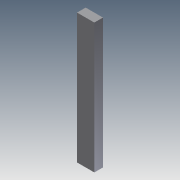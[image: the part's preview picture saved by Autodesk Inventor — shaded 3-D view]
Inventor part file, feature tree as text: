
AUTODESK INVENTOR PART (.ipt)
format: ipt  version: 2011 (Build 150239000, 239)  size: 657,920 bytes
history: native  units: in
note: dims shown in document units (in); Inventor stores cm internally (conversion verified against a paired STEP export)
features: extrude x31, sketch x31
ambient origin geometry x8: Origin, YZ Plane, XZ Plane, XY Plane, X Axis, Y Axis, Z Axis, Center Point
bodies: Solid1 (feature_tree)
feature tree (62):
  extrude  "Extrusion1"  Depth=6.75in
  extrude  "Extrusion2"  Depth=0.5in
  extrude  "Extrusion3"  Depth=0.5in
  extrude  "Extrusion4"  Depth=5.75in
  extrude  "Extrusion5"  Depth=0.5in
  extrude  "Extrusion6"  Depth=1.5in
  extrude  "Extrusion7"  Depth=1.5in
  extrude  "Extrusion8"  Depth=0.156in
  extrude  "Extrusion9"  Depth=0.25in TaperAngle=0.0deg
  extrude  "Extrusion10"  Depth=0.25in TaperAngle=0.0deg
  extrude  "Extrusion11"  Depth=0.25in TaperAngle=0.0deg
  extrude  "Extrusion12"  Depth=0.25in
  extrude  "Extrusion13"  Depth=0.25in
  extrude  "Extrusion14"  Depth=0.25in TaperAngle=0.0deg
  extrude  "Extrusion15"  Depth=3.0in
  extrude  "Extrusion16"  Depth=0.25in TaperAngle=0.0deg
  extrude  "Extrusion17"  Depth=1.0in
  extrude  "Extrusion18"  Depth=0.25in TaperAngle=0.0deg
  extrude  "Extrusion19"  Depth=0.25in TaperAngle=0.0deg
  extrude  "Extrusion20"  Depth=0.25in TaperAngle=0.0deg
  extrude  "Extrusion21"  Depth=1.0in
  extrude  "Extrusion22"  Depth=1.0in
  extrude  "Extrusion23"  Depth=2.0in
  extrude  "Extrusion24"  Depth=0.5in
  extrude  "Extrusion25"  Depth=0.5in
  extrude  "Extrusion26"  Depth=0.5in
  extrude  "Extrusion27"  Depth=0.5in
  extrude  "Extrusion28"  Depth=0.5in
  extrude  "Extrusion29"  Depth=0.5in
  extrude  "Extrusion30"  Depth=0.25in TaperAngle=0.0deg
  extrude  "Extrusion31"  Depth=1.0in
  sketch  "Sketch1"  dims[d0=5.2in d1=6.75in]
  sketch  "Sketch2"  dims[d2=0.25in d3=0.5in]
  sketch  "Sketch3"  dims[d4=5.7in d5=0.5in]
  sketch  "Sketch4"  dims[d6=0.5in d7=5.75in]
  sketch  "Sketch5"  dims[d8=0.375in d9=0.5in]
  sketch  "Sketch6"  dims[d10=0.25in d11=1.5in]
  sketch  "Sketch7"  dims[d12=0.25in d13=1.5in]
  sketch  "Sketch8"  dims[d14=0.25in d15=0.156in]
  sketch  "Sketch9"  dims[d16=0.156in d17=0.25in d18=0.0in]
  sketch  "Sketch10"  dims[d19=0.125in d20=0.0in d21=0.25in d22=0.0in]
  sketch  "Sketch11"  dims[d23=0.25in d24=0.0in d25=0.25in d26=0.0in]
  sketch  "Sketch12"  dims[d27=0.25in d28=0.25in]
  sketch  "Sketch13"  dims[d29=0.25in d30=0.25in]
  sketch  "Sketch14"  dims[d31=0.25in d32=0.25in d33=0.0in]
  sketch  "Sketch15"  dims[d34=1.5in d35=3.0in]
  sketch  "Sketch16"  dims[d36=1.0in d37=0.25in d38=0.0in]
  sketch  "Sketch17"  dims[d39=6.65in d40=1.0in]
  sketch  "Sketch18"  dims[d41=1.5in d42=0.25in d43=0.0in]
  sketch  "Sketch19"  dims[d44=0.25in d45=0.0in d46=0.25in d47=0.0in]
  sketch  "Sketch20"  dims[d48=1.0in d49=0.25in d50=0.0in]
  sketch  "Sketch21"  dims[d51=0.25in d52=1.0in]
  sketch  "Sketch22"  dims[d53=0.25in d54=1.0in]
  sketch  "Sketch23"  dims[d55=0.25in d56=2.0in]
  sketch  "Sketch24"  dims[d57=1.0in d58=0.5in]
  sketch  "Sketch25"  dims[d59=1.0in d60=0.5in]
  sketch  "Sketch26"  dims[d61=1.0in d62=0.5in]
  sketch  "Sketch27"  dims[d63=1.0in d64=0.5in]
  sketch  "Sketch28"  dims[d65=1.0in d66=0.5in]
  sketch  "Sketch29"  dims[d67=1.0in d68=0.5in]
  sketch  "Sketch30"  dims[d69=1.0in d70=0.25in d71=0.0in]
  sketch  "Sketch31"  dims[d72=0.25in d73=1.0in d74=1.0in d75=0.25in d76=0.0in d77=0.25in d78=0.0in d79=0.25in d80=0.25in d81=0.0in d82=0.75in d83=0.156in d84=0.156in d85=0.25in d86=0.0in d87=0.25in d88=0.0in d89=1.0in d90=1.0in d91=1.0in d92=0.25in d93=0.0in d94=1.0in d95=0.0in d96=1.0in d97=0.0in d98=1.0in d99=0.0in d100=0.5in d101=0.0in d102=0.5in d103=0.0in d104=0.25in d105=0.5in d106=0.0in d107=0.5in d108=0.0in d109=0.25in d110=0.0in d111=0.25in d112=0.0in d113=0.25in d114=0.5in d115=0.0in d116=0.25in d117=0.0in d118=0.5in d119=0.0in d120=0.25in d121=0.0in]
